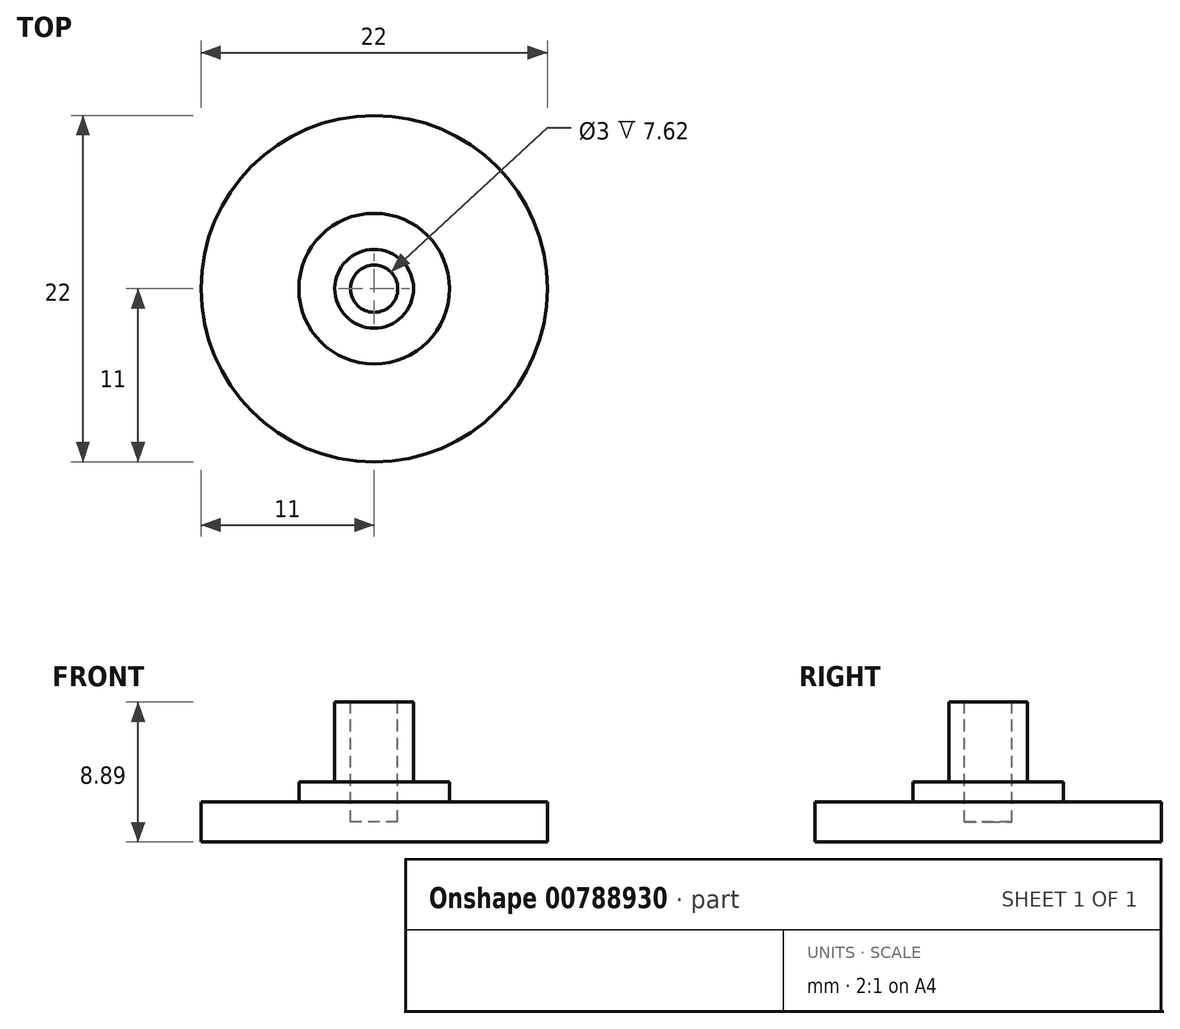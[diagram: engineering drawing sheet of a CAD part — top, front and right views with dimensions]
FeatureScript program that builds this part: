
annotation { "Feature Type Name" : "Feature", "Feature Type Description" : "" }
export const myFeature = defineFeature(function(context is Context, id is Id, definition is map)
    precondition{}
    {
        {
            var Q0;
            Q0=qCreatedBy(makeId("Top.planeOp"),FACE);
            var sketch = newSketch(context, id + "F0", { "sketchPlane" : qUnion([Q0])});
            skCircle(sketch, "E0", {"center": v(0, 0) * mm, "radius": 11 * mm});
            skCircle(sketch, "E1", {"center": v(0, 0) * mm, "radius": 4.79 * mm});
            skCircle(sketch, "E2", {"center": v(0, 0) * mm, "radius": 2.5 * mm});
            skSolve(sketch);
        }
        {
            var Q0;
            Q0=makeQuery(id+"F0.imprint","IMPRINT",FACE,{"disambiguationData":[TD([[makeQuery(id+"F0.imprint","IMPRINT",EDGE,{"derivedFrom":sQuery(id+"F0.wireOp",EDGE,"E2")}),1.0]])]});
            extrude(context, id + "F1", {"entities" : qUnion([Q0]), "depth" : 8.9 * mm, "offsetDistance" : 25.4 * mm});
        }
        {
            var Q0;
            Q0=makeQuery(id+"F0.imprint","IMPRINT",FACE,{"disambiguationData":[TD([[makeQuery(id+"F0.imprint","IMPRINT",EDGE,{"derivedFrom":sQuery(id+"F0.wireOp",EDGE,"E1")}),1.0]])]});
            extrude(context, id + "F2", {"entities" : qUnion([Q0]), "operationType" : NewBodyOperationType.ADD, "depth" : 3.8 * mm, "offsetDistance" : 25.4 * mm});
        }
        {
            var Q0;
            Q0=makeQuery(id+"F0.imprint","IMPRINT",FACE,{"disambiguationData":[TD([[makeQuery(id+"F0.imprint","IMPRINT",EDGE,{"derivedFrom":sQuery(id+"F0.wireOp",EDGE,"E0")}),1.0]])]});
            extrude(context, id + "F3", {"entities" : qUnion([Q0]), "operationType" : NewBodyOperationType.ADD, "depth" : 2.54 * mm, "offsetDistance" : 25.4 * mm});
        }
        {
            var Q0;
            Q0=makeQuery(id+"F1.opExtrude","CAP_FACE",FACE,{"disambiguationData":[OSD([sQuery(id+"F0.wireOp",EDGE,"E2")])],"isStart":false});
            var sketch = newSketch(context, id + "F4", { "sketchPlane" : qUnion([Q0])});
            skCircle(sketch, "E3", {"center": v(0, 0) * mm, "radius": 1.5 * mm});
            skSolve(sketch);
        }
        {
            var Q0;
            Q0=makeQuery(id+"F4.imprint","IMPRINT",FACE,{"disambiguationData":[TD([[makeQuery(id+"F4.imprint","IMPRINT",EDGE,{"derivedFrom":sQuery(id+"F4.wireOp",EDGE,"E3")}),1.0]])]});
            extrude(context, id + "F5", {"entities" : qUnion([Q0]), "operationType" : NewBodyOperationType.REMOVE, "oppositeDirection" : true, "depth" : 7.62 * mm, "offsetDistance" : 25.4 * mm});
        }
    });
